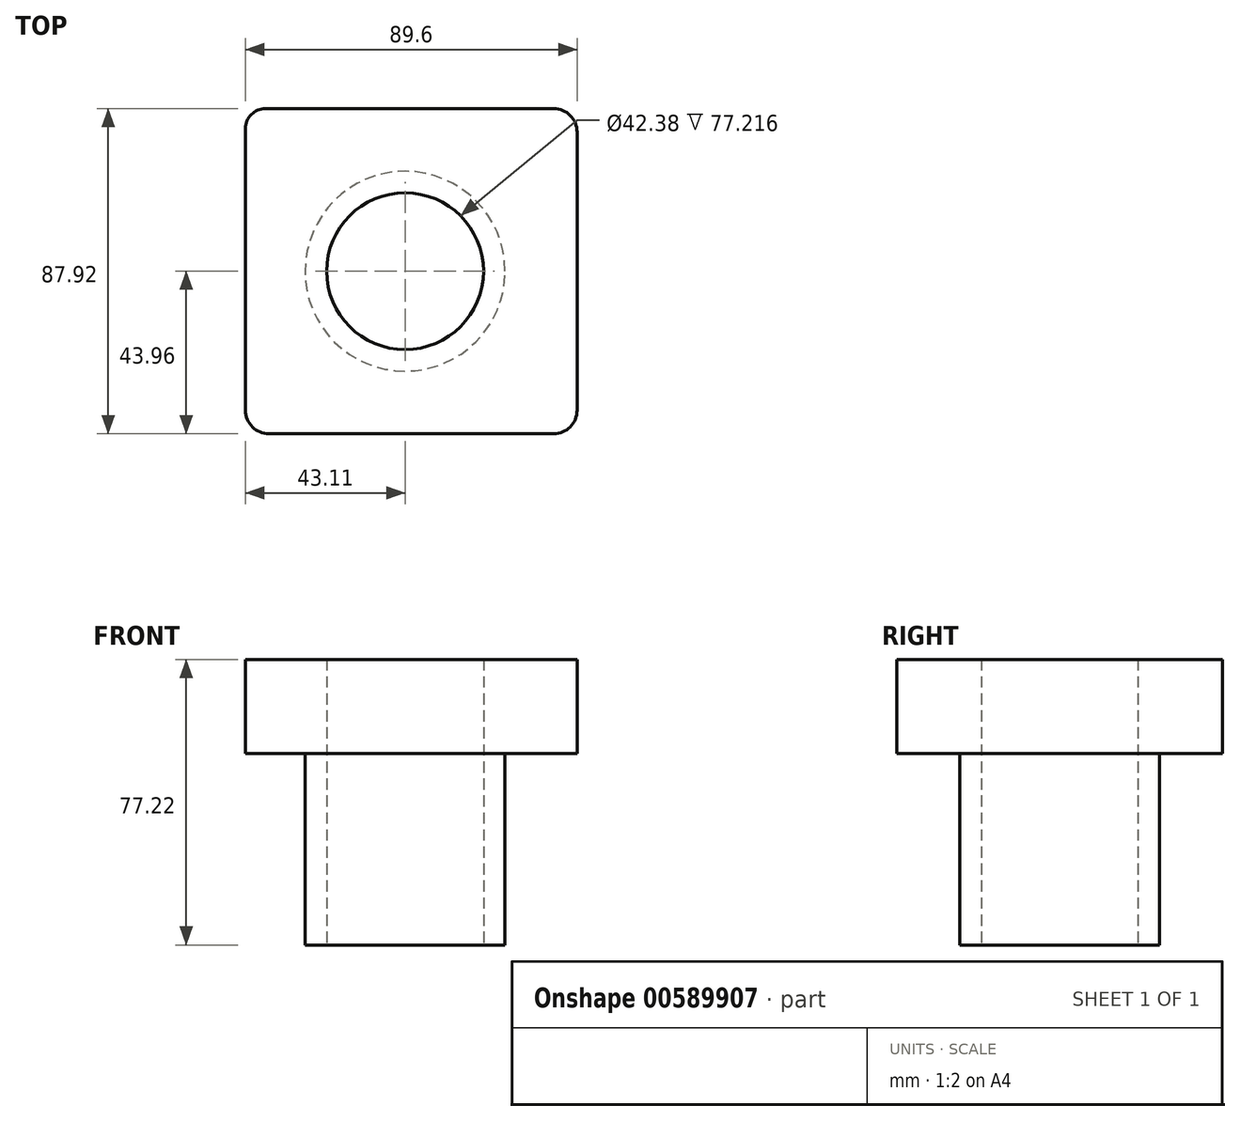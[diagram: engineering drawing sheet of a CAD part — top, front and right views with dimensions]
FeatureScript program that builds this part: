
annotation { "Feature Type Name" : "Feature", "Feature Type Description" : "" }
export const myFeature = defineFeature(function(context is Context, id is Id, definition is map)
    precondition{}
    {
        {
            var Q0;
            Q0=qCreatedBy(makeId("Top.planeOp"),FACE);
            var sketch = newSketch(context, id + "F0", { "sketchPlane" : qUnion([Q0])});
            skLineSegment(sketch, "E0.bottom", {"start": v(-38.45, -43.96) * mm, "end": v(38.45, -43.96) * mm});
            skLineSegment(sketch, "E0.top", {"start": v(-39.43, 43.96) * mm, "end": v(38.45, 43.96) * mm});
            skLineSegment(sketch, "E0.left", {"start": v(-44.8, -37.61) * mm, "end": v(-44.8, 38.59) * mm});
            skLineSegment(sketch, "E0.right", {"start": v(44.8, -37.61) * mm, "end": v(44.8, 37.61) * mm});
            skPoint(sketch, "E0.middle", {"position": v(0, 0) * mm});
            skCircle(sketch, "E1", {"center": v(-1.69, 0) * mm, "radius": 21.2 * mm});
            skPoint(sketch, "E2.visualSharp", {"position": v(-44.8, -43.96) * mm});
            skArc(sketch, "E2.filletArc", {"start": v(-44.8, -37.61) * mm, "mid": v(-42.94, -42.1) * mm, "end": v(-38.45, -43.96) * mm});
            skPoint(sketch, "E3.visualSharp", {"position": v(44.8, -43.96) * mm});
            skArc(sketch, "E3.filletArc", {"start": v(38.45, -43.96) * mm, "mid": v(42.94, -42.1) * mm, "end": v(44.8, -37.61) * mm});
            skPoint(sketch, "E4.visualSharp", {"position": v(44.8, 43.96) * mm});
            skArc(sketch, "E4.filletArc", {"start": v(44.8, 37.61) * mm, "mid": v(42.94, 42.1) * mm, "end": v(38.45, 43.96) * mm});
            skPoint(sketch, "E5.visualSharp", {"position": v(-44.8, 43.96) * mm});
            skArc(sketch, "E5.filletArc", {"start": v(-39.43, 43.96) * mm, "mid": v(-43.22, 42.39) * mm, "end": v(-44.8, 38.59) * mm});
            skSolve(sketch);
        }
        {
            var Q0;
            Q0 = qSketchRegion(id + "F0", true);
            extrude(context, id + "F1", {"entities" : qUnion([Q0]), "depth" : 25.4 * mm, "offsetDistance" : 25.4 * mm});
        }
        {
            var Q0;
            Q0=qCreatedBy(makeId("Top.planeOp"),FACE);
            var sketch = newSketch(context, id + "F2", { "sketchPlane" : qUnion([Q0])});
            skCircle(sketch, "E6.0", {"center": v(-1.69, 0) * mm, "radius": 21.2 * mm});
            skCircle(sketch, "E7", {"center": v(-1.69, 0) * mm, "radius": 27.02 * mm});
            skSolve(sketch);
        }
        {
            var Q0;
            Q0 = qSketchRegion(id + "F2", true);
            extrude(context, id + "F3", {"entities" : qUnion([Q0]), "operationType" : NewBodyOperationType.ADD, "oppositeDirection" : true, "depth" : 51.82 * mm, "offsetDistance" : 25.4 * mm});
        }
    });
